# Revit family: 604281711_Mueble Aluvia Miel 45X45
name_source: partatom
category: Plumbing Fixtures
units: mm (PartAtom-declared; Revit-internal decimal feet)

## family parameters
Always vertical = Yes
Cut with Voids When Loaded = No
OmniClass Number = 23.31.13.11
OmniClass Title = Single Sinks
Part Type = Normal
Room Calculation Point = No
Round Connector Dimension = Use Diameter
Shared = No
Work Plane-Based = Yes

## types (2) — shared parameters
Alto = 850 mm  [stored 2.78871 ft]
Ancho = 445 mm  [stored 1.45997 ft]
Canto = PVC rígido 2 mm de calibre.
Carga máxima = 99,2 lb (45 kg).
Default Elevation = 1219 mm
Densidad = 15 mms 670 kg./m^3.
Description = La línea ALUVIA viene a entregar de manera asequible una solución perfecta que combina
diseño y funcionalidad, ALUVIA se inspira en el movimiento y caída del agua en la
naturaleza, es por ello de sus formas orgánicas donde podemos obtener un producto
compacto y de líneas fluidas, que se adapta en espacios pequeños.
el pricipal benefico de los muebles de esta linea es ser un producto compacto que cuenta
con cajón y repisa brindándole al consumidor mayor capacidad de almacenamiento, como
una excelente solución para aquellos espacios pequeños.
· Mueble compacto para espacios pequeños.
· Lavamanos 100% en porcelana.
· Grán capacidad de almacenamiento.
Dimensiones Generales (H * W * P) = 33,46” x 17,51” x 17,51” (850 x 445 x 445 mm).
Garantia Herrajes = 1 año
Garantia Madera = 1 año
Manufacturer = Corona
Material Lavamanos = Corona_Cerámica_Sinterizada
Material madera interior = Corona_Madera_Aglomerada_Plomo
Model = Mueble aluvia miel LVM 45X45
Patas = Corona_Acero
Peso Bruto aprox = 43,4 lb (19,69 kg).
Peso Neto aprox = 41 lb (18,6 kg).
Pieza en U = Corona_Poliestrieno_Gris
Resistencia a la humedad = 8%
Resistencia al rayado = 700 ciclos

## per-type parameters (varying)
| type | Material | Profundidad | URL |
| Ref. 604281711 Mueble Aluvia Miel Con Lavamanos | Corona_Madera_Aglomerada_Miel | 430 mm | https://corona.co |
| Ref. 604286091 Mueble Aluvia Habano Con Lavamanos | Corona_Madera_Aglomerada_Habano | 440 mm  [stored 1.44357 ft] |  |

note: [stored X ft] marks values corroborated as IEEE doubles in the binary element streams (Revit-internal decimal feet)

## geometry (parser evidence)
native form markers: Sweep x19
no freeform markers — native parametric forms only
